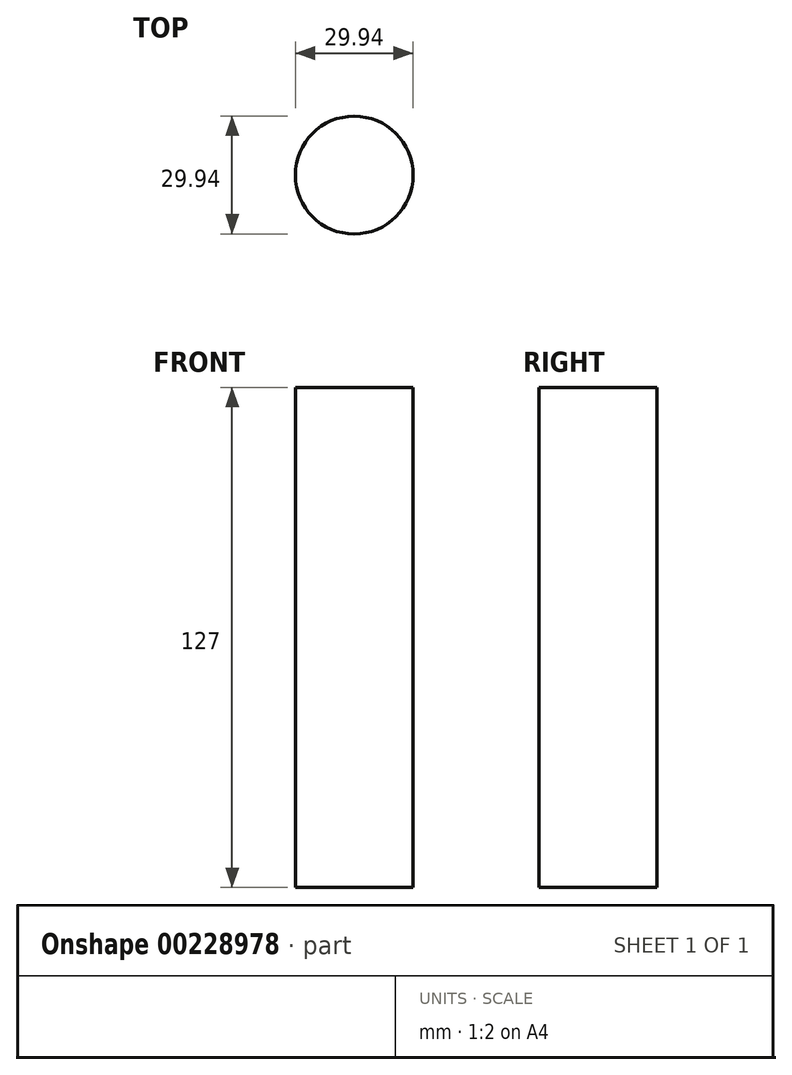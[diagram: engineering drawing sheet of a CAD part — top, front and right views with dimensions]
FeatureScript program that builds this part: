
annotation { "Feature Type Name" : "Feature", "Feature Type Description" : "" }
export const myFeature = defineFeature(function(context is Context, id is Id, definition is map)
    precondition{}
    {
        {
            var Q0;
            Q0=qCreatedBy(makeId("Top.planeOp"),FACE);
            var sketch = newSketch(context, id + "F0", { "sketchPlane" : qUnion([Q0])});
            skCircle(sketch, "E0", {"center": v(0, 0) * mm, "radius": 14.97 * mm});
            skSolve(sketch);
        }
        {
            var Q0;
            Q0 = qSketchRegion(id + "F0", true);
            extrude(context, id + "F1", {"entities" : qUnion([Q0]), "depth" : 127 * mm});
        }
    });
